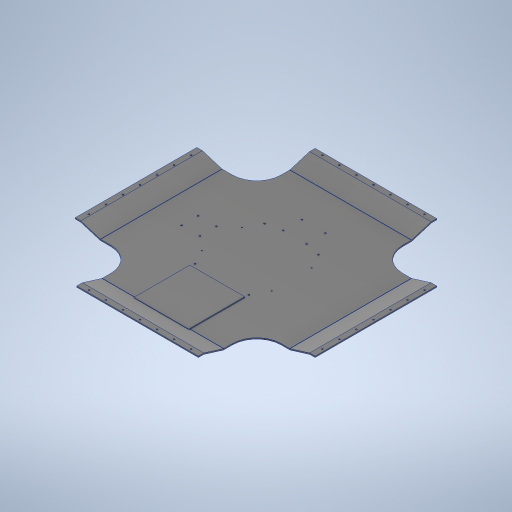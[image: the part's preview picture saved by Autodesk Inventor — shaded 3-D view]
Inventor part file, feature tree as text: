
AUTODESK INVENTOR PART (.ipt)
format: ipt  version: 2024.2 (Build 282272000, 272)  size: 861,184 bytes
history: native  units: in
note: dims shown in document units (in); Inventor stores cm internally (conversion verified against a paired STEP export)
features: extrude x13, sketch x13, projected_geometry x10, fillet x1
ambient origin geometry x8: Origin, YZ Plane, XZ Plane, XY Plane, X Axis, Y Axis, Z Axis, Center Point
bodies: Body1 (feature_tree)
feature tree (37):
  extrude  "Extrusion5"  Depth=24.5in
  extrude  "Extrusion6"  Depth=0.5in
  extrude  "Extrusion8"  Depth=1.5748in
  extrude  "Extrusion17"  Depth=1.5748in
  extrude  "Extrusion18"  Depth=2.5in
  sketch  "Sketch19"  dims[d94=2.4375in d95=0.0in d144=0.371in]
  extrude  "Extrusion19"  Depth=0.371in
  extrude  "Extrusion20"  Depth=0.55in
  extrude  "Extrusion21"  Depth=0.5in
  fillet  "Fillet1"  Radius=1.0in
  extrude  "Extrusion24"  Depth=1.696in
  extrude  "Extrusion26"  Depth=0.5in
  extrude  "Extrusion27"  Depth=1.0in TaperAngle=0.0deg
  extrude  "Extrusion28"  Depth=4.375in TaperAngle=0.0deg
  extrude  "Extrusion29"  Depth=0.1in
  sketch  "Sketch6"  dims[d60=24.5in d61=24.5in]
  sketch  "Sketch7"  dims[d62=0.125in d63=0.0in d64=0.5in]
  projected_geometry  "Projected Loop2"
  sketch  "Sketch8"  dims[d65=0.157in d66=1.5748in d68=1.75in d69=1.5748in d71=1.75in]
  projected_geometry  "Projected Loop3"
  sketch  "Sketch17"  dims[d74=0.157in d75=1.5748in d77=1.75in d78=1.5748in d80=1.75in]
  projected_geometry  "Projected Loop85"
  projected_geometry  "Projected Loop86"
  sketch  "Sketch18"  dims[d83=0.125in d84=0.0in d93=2.5in]
  projected_geometry  "Projected Loop87"
  projected_geometry  "Projected Loop88"
  projected_geometry  "Projected Loop89"
  projected_geometry  "Projected Loop90"
  projected_geometry  "Projected Loop91"
  projected_geometry  "Projected Loop92"
  sketch  "Sketch20"  dims[d150=0.55in d151=0.55in]
  sketch  "Sketch21"  dims[d152=0.125in d153=0.5in d154=1.0in d155=0.0in]
  sketch  "Sketch24"  dims[d157=0.55in d158=1.696in]
  sketch  "Sketch26"  dims[d159=0.125in d160=0.5in]
  sketch  "Sketch27"  dims[d161=1.0in d162=0.0in d163=1.0in d164=0.0in]
  sketch  "Sketch28"  dims[d165=15.625in d166=0.0in d167=4.375in d168=0.0in]
  sketch  "Sketch29"  dims[d169=0.125in d174=5.533in d175=7.153in d176=0.157in d177=0.157in d178=0.157in d179=0.157in d180=1.1875in d181=0.0in d184=7.176in d185=4.11in d186=0.106in d187=0.106in d188=0.106in d189=0.625in d190=0.0in d191=2.403in d192=1.923in d193=0.149in d194=0.149in d195=1.6875in d196=0.0in d197=1.88in d198=1.695in d199=0.157in d200=0.157in d201=0.157in d202=0.157in d203=0.4375in d204=0.0in d205=5.637in d206=5.754in d207=0.1in d208=0.0in]
